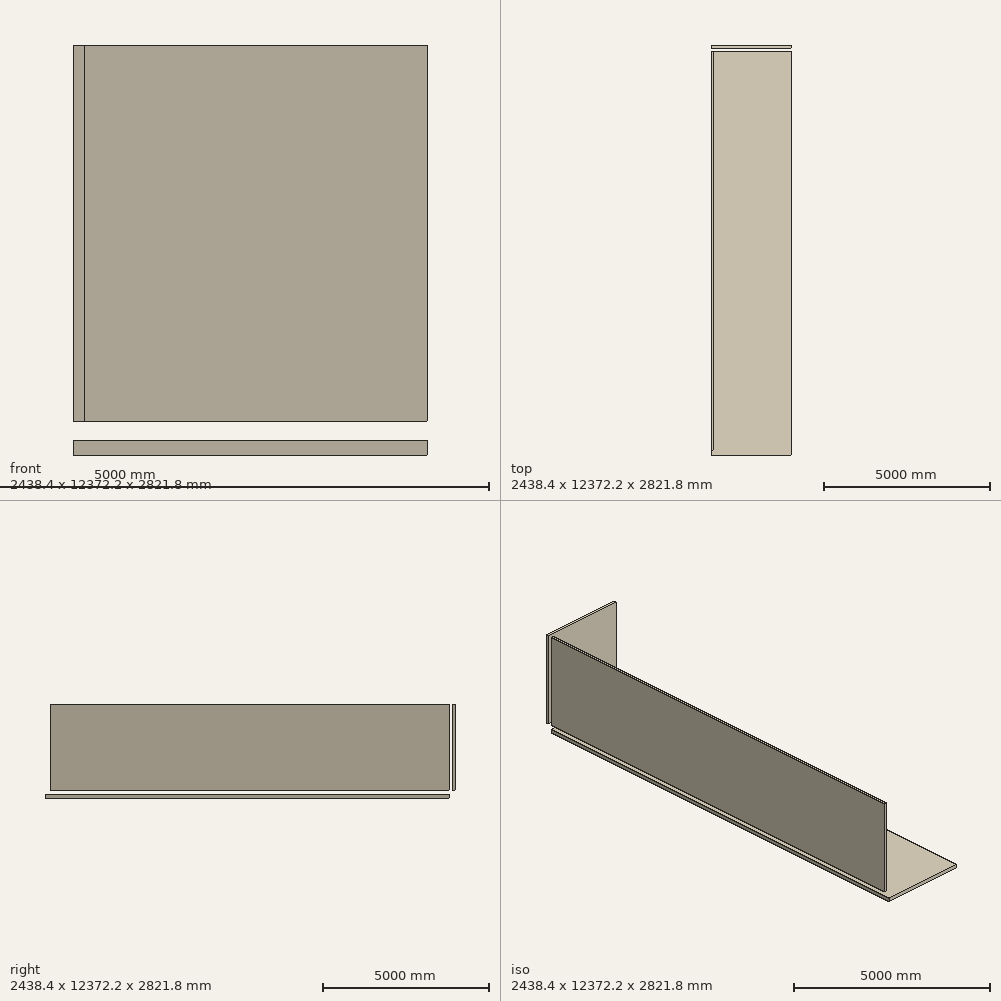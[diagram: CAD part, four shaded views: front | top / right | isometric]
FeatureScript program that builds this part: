
annotation { "Feature Type Name" : "Feature", "Feature Type Description" : "" }
export const myFeature = defineFeature(function(context is Context, id is Id, definition is map)
    precondition{}
    {
        {
            var Q0;
            Q0=qCreatedBy(makeId("Front.planeOp"),FACE);
            var sketch = newSketch(context, id + "F0", { "sketchPlane" : qUnion([Q0])});
            skLineSegment(sketch, "E0.bottom", {"start": v(0, 0) * mm, "end": v(76.2, 0) * mm});
            skLineSegment(sketch, "E0.top", {"start": v(0, 2590.8) * mm, "end": v(76.2, 2590.8) * mm});
            skLineSegment(sketch, "E0.left", {"start": v(0, 0) * mm, "end": v(0, 2590.8) * mm});
            skLineSegment(sketch, "E0.right", {"start": v(76.2, 0) * mm, "end": v(76.2, 2590.8) * mm});
            skSolve(sketch);
        }
        {
            var Q0;
            Q0 = qSketchRegion(id + "F0", true);
            extrude(context, id + "F1", {"entities" : qUnion([Q0]), "depth" : 12039.6 * mm, "offsetDistance" : 25.4 * mm});
        }
        {
            var Q0;
            Q0=qCreatedBy(makeId("Right.planeOp"),FACE);
            var sketch = newSketch(context, id + "F2", { "sketchPlane" : qUnion([Q0])});
            skLineSegment(sketch, "E1.bottom", {"start": v(104, 0) * mm, "end": v(180.2, 0) * mm});
            skLineSegment(sketch, "E1.top", {"start": v(104, 2590.8) * mm, "end": v(180.2, 2590.8) * mm});
            skLineSegment(sketch, "E1.left", {"start": v(104, 0) * mm, "end": v(104, 2590.8) * mm});
            skLineSegment(sketch, "E1.right", {"start": v(180.2, 0) * mm, "end": v(180.2, 2590.8) * mm});
            skSolve(sketch);
        }
        {
            var Q0;
            Q0 = qSketchRegion(id + "F2", true);
            extrude(context, id + "F3", {"entities" : qUnion([Q0]), "depth" : 2438.4 * mm, "offsetDistance" : 25.4 * mm});
        }
        {
            var Q0;
            Q0=qCreatedBy(makeId("Front.planeOp"),FACE);
            var sketch = newSketch(context, id + "F4", { "sketchPlane" : qUnion([Q0])});
            skLineSegment(sketch, "E2.bottom", {"start": v(2438.4, -231.03) * mm, "end": v(0, -231.03) * mm});
            skLineSegment(sketch, "E2.top", {"start": v(2438.4, -129.43) * mm, "end": v(0, -129.43) * mm});
            skLineSegment(sketch, "E2.left", {"start": v(2438.4, -231.03) * mm, "end": v(2438.4, -129.43) * mm});
            skLineSegment(sketch, "E2.right", {"start": v(0, -231.03) * mm, "end": v(0, -129.43) * mm});
            skSolve(sketch);
        }
        {
            var Q0;
            Q0=makeQuery(id+"F4.imprint","IMPRINT",FACE,{"disambiguationData":[TD([[makeQuery(id+"F4.imprint","IMPRINT",EDGE,{"derivedFrom":sQuery(id+"F4.wireOp",EDGE,"E2.bottom")}),-1.0]])]});
            extrude(context, id + "F5", {"entities" : qUnion([Q0]), "depth" : 12192 * mm, "offsetDistance" : 25.4 * mm});
        }
    });
